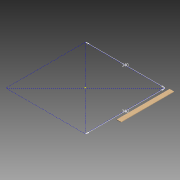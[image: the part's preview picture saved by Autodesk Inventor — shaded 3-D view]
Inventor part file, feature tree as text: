
AUTODESK INVENTOR PART (.ipt)
format: ipt  version: 2013 SP1 (Build 170176100, 176)  size: 92,160 bytes
history: native  units: mm
features: sketch x2, extrude x1, other x1
ambient origin geometry x8: Origin, YZ Plane, XZ Plane, XY Plane, X Axis, Y Axis, Z Axis, Center Point
bodies: Volumenkörper1 (feature_tree)
feature tree (4):
  sketch  "Skizze Helper"  dims[d2=2.0mm d3=0.0mm d4=0.0mm d5=0.0mm d6=-2.0mm]
  extrude  "Extrusion1"  Depth=340.0mm
  other  "Körper verschieben1"
  sketch  "Skizze2"  dims[d0=340.0mm d1=340.0mm]
